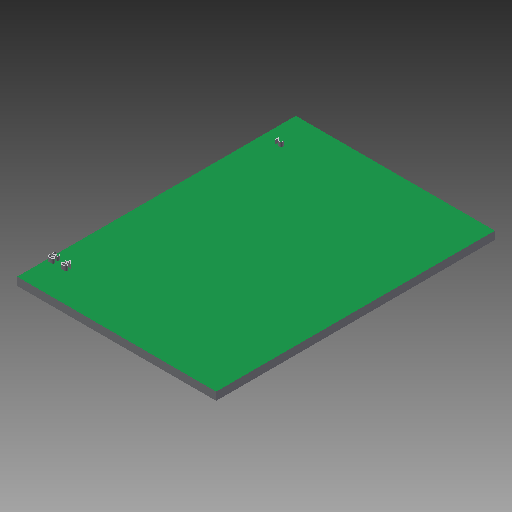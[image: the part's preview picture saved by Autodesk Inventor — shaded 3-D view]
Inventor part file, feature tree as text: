
AUTODESK INVENTOR PART (.ipt)
format: ipt  version: 2017 (Build 210142000, 142)  size: 271,872 bytes
history: native  units: in
note: dims shown in document units (in); Inventor stores cm internally (conversion verified against a paired STEP export)
features: sketch x2, extrude x1, emboss x1
ambient origin geometry x8: Origin, YZ Plane, XZ Plane, XY Plane, X Axis, Y Axis, Z Axis, Center Point
bodies: Solid1 (feature_tree)
feature tree (4):
  extrude  "Extrusion1"  Depth=1.9685in
  emboss  "Emboss1"
  sketch  "Sketch1"  dims[d0=2.7559in d1=1.9685in]
  sketch  "Sketch2"  dims[d2=0.0787in d3=0.0in d4=0.0394in d5=0.0in]
